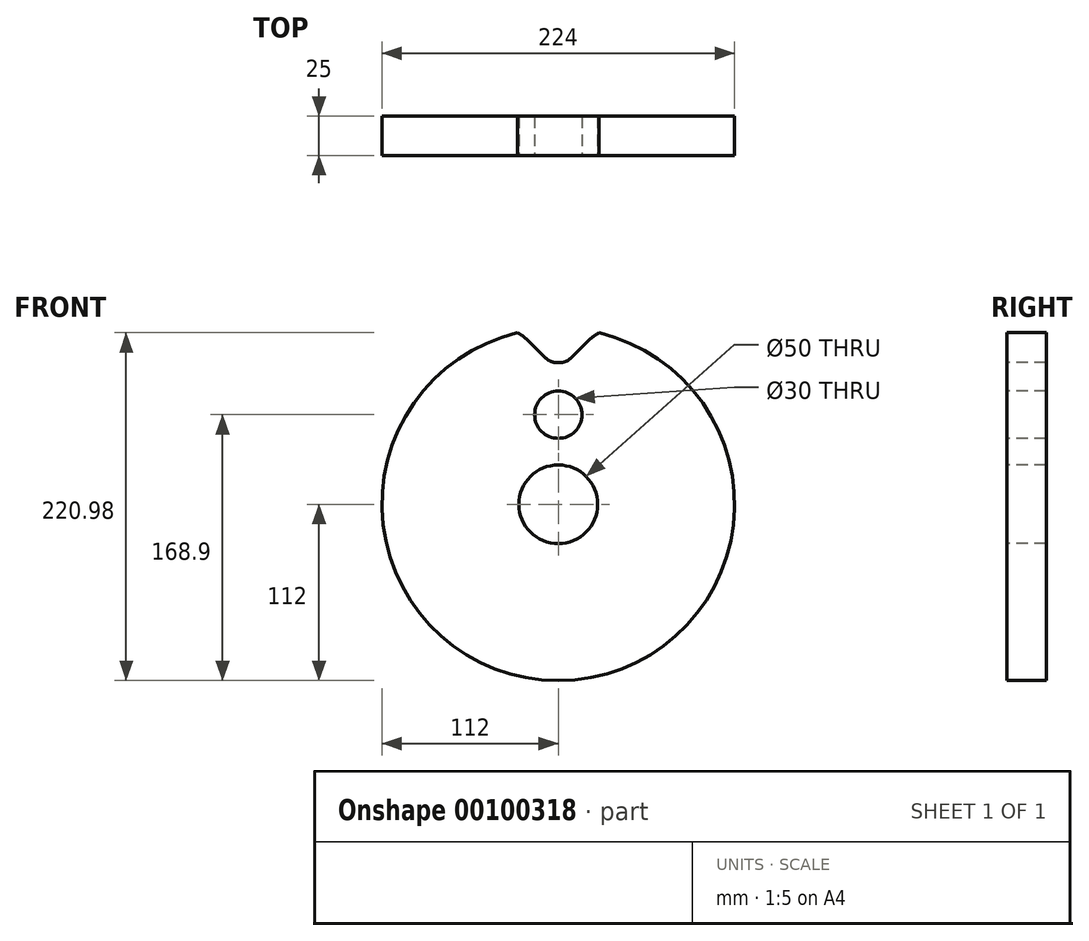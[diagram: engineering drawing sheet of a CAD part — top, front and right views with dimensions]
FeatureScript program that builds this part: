
annotation { "Feature Type Name" : "Feature", "Feature Type Description" : "" }
export const myFeature = defineFeature(function(context is Context, id is Id, definition is map)
    precondition{}
    {
        {
            var Q0;
            Q0=qCreatedBy(makeId("Front.planeOp"),FACE);
            var sketch = newSketch(context, id + "F0", { "sketchPlane" : qUnion([Q0])});
            skCircle(sketch, "E0.cCircle", {"center": v(0, 0) * mm, "radius": 100 * mm, "construction": true});
            skLineSegment(sketch, "E0.0", {"start": v(0, 100) * mm, "end": v(29.48, 95.56) * mm});
            skLineSegment(sketch, "E0.1", {"start": v(29.48, 95.56) * mm, "end": v(56.33, 82.62) * mm});
            skLineSegment(sketch, "E0.2", {"start": v(56.33, 82.62) * mm, "end": v(78.18, 62.35) * mm});
            skLineSegment(sketch, "E0.3", {"start": v(78.18, 62.35) * mm, "end": v(93.09, 36.53) * mm});
            skLineSegment(sketch, "E0.4", {"start": v(93.09, 36.53) * mm, "end": v(99.72, 7.47) * mm});
            skLineSegment(sketch, "E0.5", {"start": v(99.72, 7.47) * mm, "end": v(97.5, -22.25) * mm});
            skLineSegment(sketch, "E0.6", {"start": v(97.5, -22.25) * mm, "end": v(86.6, -50) * mm});
            skLineSegment(sketch, "E0.7", {"start": v(86.6, -50) * mm, "end": v(68.02, -73.3) * mm});
            skLineSegment(sketch, "E0.8", {"start": v(68.02, -73.3) * mm, "end": v(43.39, -90.1) * mm});
            skLineSegment(sketch, "E0.9", {"start": v(43.39, -90.1) * mm, "end": v(14.9, -98.88) * mm});
            skLineSegment(sketch, "E0.10", {"start": v(14.9, -98.88) * mm, "end": v(-14.9, -98.88) * mm});
            skLineSegment(sketch, "E0.11", {"start": v(-14.9, -98.88) * mm, "end": v(-43.39, -90.1) * mm});
            skLineSegment(sketch, "E0.12", {"start": v(-43.39, -90.1) * mm, "end": v(-68.02, -73.3) * mm});
            skLineSegment(sketch, "E0.13", {"start": v(-68.02, -73.3) * mm, "end": v(-86.6, -50) * mm});
            skLineSegment(sketch, "E0.14", {"start": v(-86.6, -50) * mm, "end": v(-97.5, -22.25) * mm});
            skLineSegment(sketch, "E0.15", {"start": v(-97.5, -22.25) * mm, "end": v(-99.72, 7.47) * mm});
            skLineSegment(sketch, "E0.16", {"start": v(-99.72, 7.47) * mm, "end": v(-93.09, 36.53) * mm});
            skLineSegment(sketch, "E0.17", {"start": v(-93.09, 36.53) * mm, "end": v(-78.18, 62.35) * mm});
            skLineSegment(sketch, "E0.18", {"start": v(-78.18, 62.35) * mm, "end": v(-56.33, 82.62) * mm});
            skLineSegment(sketch, "E0.19", {"start": v(-56.33, 82.62) * mm, "end": v(-29.48, 95.56) * mm});
            skLineSegment(sketch, "E0.20", {"start": v(-29.48, 95.56) * mm, "end": v(0, 100) * mm});
            skLineSegment(sketch, "E1", {"start": v(0, 0) * mm, "end": v(0, 100) * mm, "construction": true});
            skArc(sketch, "E2", {"start": v(-9, 99.6) * mm, "mid": v(-8.96, 99.12) * mm, "end": v(-8.91, 98.66) * mm});
            skCircle(sketch, "E3", {"center": v(0, 0) * mm, "radius": 90 * mm});
            skArc(sketch, "E4", {"start": v(20.26, 104.86) * mm, "mid": v(22.9, 107.11) * mm, "end": v(25.84, 108.98) * mm});
            skLineSegment(sketch, "E5", {"start": v(20.26, 104.86) * mm, "end": v(8, 92.85) * mm});
            skCircle(sketch, "E6", {"center": v(0, 0) * mm, "radius": 112 * mm});
            skArc(sketch, "E7.trimOffspring", {"start": v(0.9, 90) * mm, "mid": v(4.73, 90.72) * mm, "end": v(8, 92.85) * mm});
            skLineSegment(sketch, "E8.MirrorCS", {"start": v(-20.26, 104.86) * mm, "end": v(-8, 92.85) * mm});
            skArc(sketch, "E9.MirrorCS", {"start": v(-0.9, 90) * mm, "mid": v(-4.73, 90.72) * mm, "end": v(-8, 92.85) * mm});
            skArc(sketch, "E10.MirrorCS", {"start": v(-20.26, 104.86) * mm, "mid": v(-22.9, 107.11) * mm, "end": v(-25.84, 108.98) * mm});
            skSolve(sketch);
        }
        {
            var Q0;
            Q0 = qSketchRegion(id + "F0", true);
            var Q1;
            {var subQ0=sQuery(id+"F0.wireOp",EDGE,"E3");var subQ1=makeQuery(id+"F0.imprint","INTERSECT",VERTEX,{"derivedFrom":[subQ0,sQuery(id+"F0.wireOp",EDGE,"E7.trimOffspring")]});Q1=makeQuery(id+"F0.imprint","IMPRINT",FACE,{"disambiguationData":[TD([[makeQuery(id+"F0.imprint","IMPRINT",EDGE,{"disambiguationData":[TD([[subQ1,-1.0]])],"derivedFrom":subQ0}),1.0]])]});}
            var Q2;
            {var subQ7=sQuery(id+"F0.wireOp",EDGE,"E0.1");Q2=makeQuery(id+"F0.imprint","IMPRINT",FACE,{"disambiguationData":[TD([[makeQuery(id+"F0.imprint","IMPRINT",EDGE,{"derivedFrom":subQ7}),-1.0]])]});}
            var Q3;
            {var subQ0=sQuery(id+"F0.wireOp",EDGE,"E7.trimOffspring");Q3=makeQuery(id+"F0.imprint","IMPRINT",FACE,{"disambiguationData":[TD([[makeQuery(id+"F0.imprint","IMPRINT",EDGE,{"derivedFrom":subQ0}),1.0]])]});}
            extrude(context, id + "F1", {"entities" : qUnion([Q0, Q1, Q2, Q3]), "depth" : 25 * mm});
        }
        {
            var Q0;
            Q0=makeQuery(id+"F1.opExtrude","CAP_FACE",FACE,{"disambiguationData":[OSD([sQuery(id+"F0.wireOp",EDGE,"E6")])],"isStart":false});
            var sketch = newSketch(context, id + "F2", { "sketchPlane" : qUnion([Q0])});
            skArc(sketch, "E11.0", {"start": v(-20.26, 104.86) * mm, "mid": v(-22.9, 107.11) * mm, "end": v(-25.84, 108.98) * mm});
            skLineSegment(sketch, "E12.0", {"start": v(-20.26, 104.86) * mm, "end": v(-8, 92.85) * mm});
            skArc(sketch, "E13.0", {"start": v(-0.9, 90) * mm, "mid": v(-4.73, 90.72) * mm, "end": v(-8, 92.85) * mm});
            skArc(sketch, "E14.0", {"start": v(0.9, 90) * mm, "mid": v(0, 90) * mm, "end": v(-0.9, 90) * mm});
            skArc(sketch, "E15.0", {"start": v(0.9, 90) * mm, "mid": v(4.73, 90.72) * mm, "end": v(8, 92.85) * mm});
            skLineSegment(sketch, "E16.0", {"start": v(20.26, 104.86) * mm, "end": v(8, 92.85) * mm});
            skArc(sketch, "E17.0", {"start": v(20.26, 104.86) * mm, "mid": v(22.9, 107.11) * mm, "end": v(25.84, 108.98) * mm});
            skArc(sketch, "E18.0", {"start": v(25.84, 108.98) * mm, "mid": v(0, 112) * mm, "end": v(-25.84, 108.98) * mm});
            skSolve(sketch);
        }
        {
            var Q0;
            Q0 = qSketchRegion(id + "F2", true);
            extrude(context, id + "F3", {"entities" : qUnion([Q0]), "operationType" : NewBodyOperationType.REMOVE, "endBound" : BoundingType.THROUGH_ALL, "oppositeDirection" : true, "depth" : 25 * mm});
        }
        {
            var Q0;
            Q0=makeQuery(id+"F1.opExtrude","CAP_FACE",FACE,{"disambiguationData":[OSD([sQuery(id+"F0.wireOp",EDGE,"E6")])],"isStart":false});
            var sketch = newSketch(context, id + "F4", { "sketchPlane" : qUnion([Q0])});
            skCircle(sketch, "E19", {"center": v(0, 0) * mm, "radius": 25 * mm});
            skSolve(sketch);
        }
        {
            var Q0;
            Q0 = qSketchRegion(id + "F4", true);
            extrude(context, id + "F5", {"entities" : qUnion([Q0]), "operationType" : NewBodyOperationType.REMOVE, "endBound" : BoundingType.THROUGH_ALL, "oppositeDirection" : true, "depth" : 25 * mm});
        }
        {
            var Q0;
            Q0=makeQuery(id+"F1.opExtrude","CAP_FACE",FACE,{"disambiguationData":[OSD([sQuery(id+"F0.wireOp",EDGE,"E6")])],"isStart":false});
            var sketch = newSketch(context, id + "F6", { "sketchPlane" : qUnion([Q0])});
            skCircle(sketch, "E20", {"center": v(0, 56.9) * mm, "radius": 15 * mm});
            skSolve(sketch);
        }
        {
            var Q0;
            Q0 = qSketchRegion(id + "F6", true);
            extrude(context, id + "F7", {"entities" : qUnion([Q0]), "operationType" : NewBodyOperationType.REMOVE, "endBound" : BoundingType.THROUGH_ALL, "oppositeDirection" : true, "depth" : 25 * mm});
        }
    });
